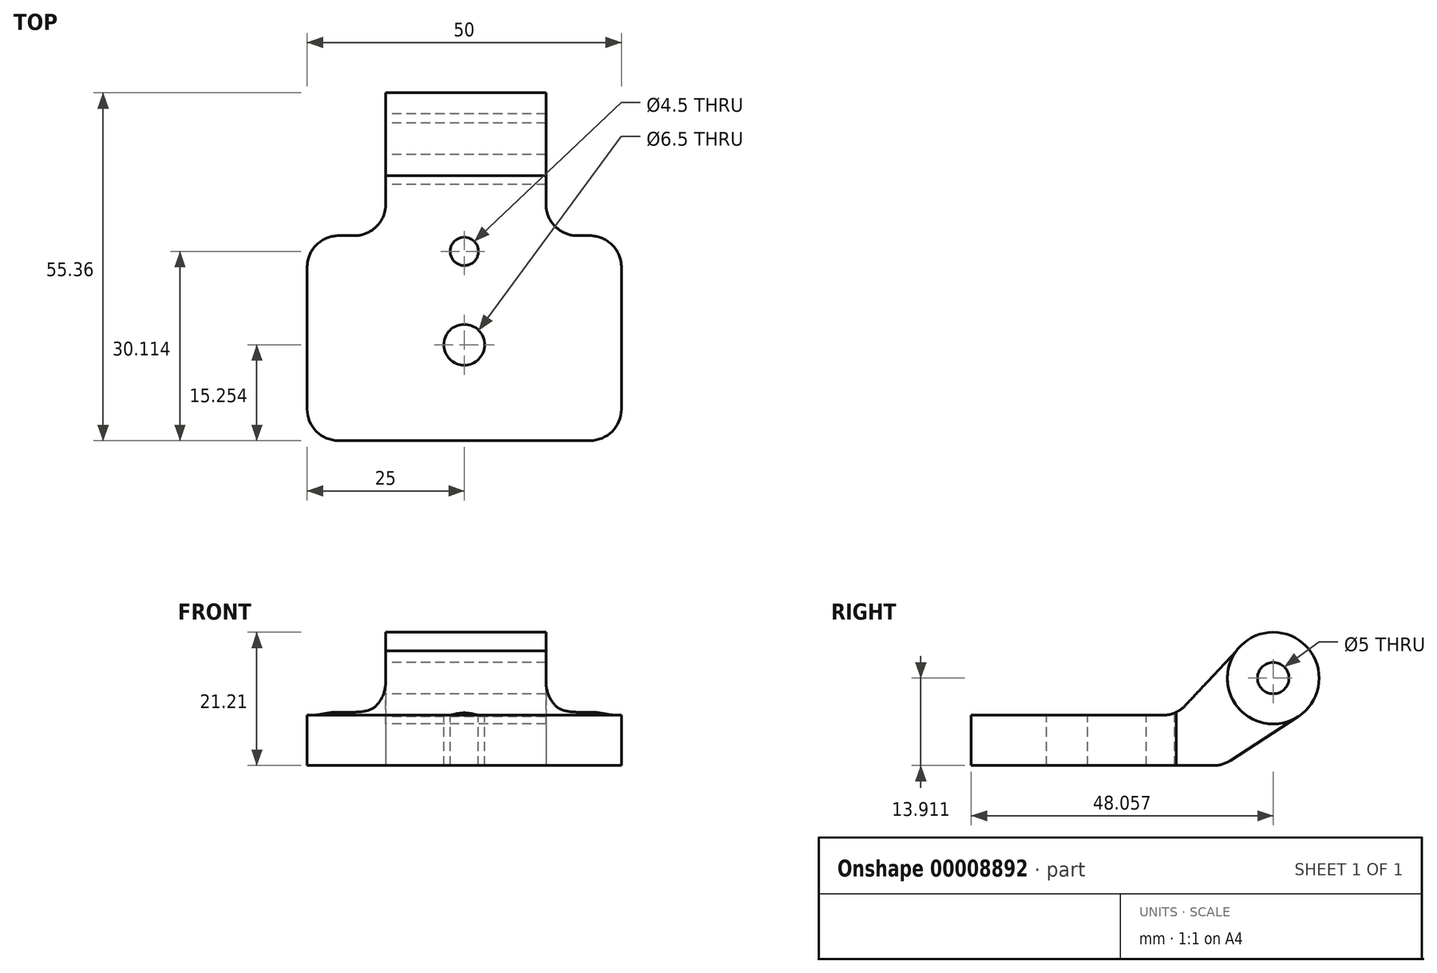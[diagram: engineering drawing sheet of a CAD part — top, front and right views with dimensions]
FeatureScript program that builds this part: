
annotation { "Feature Type Name" : "Feature", "Feature Type Description" : "" }
export const myFeature = defineFeature(function(context is Context, id is Id, definition is map)
    precondition{}
    {
        {
            var Q0;
            Q0=qCreatedBy(makeId("Right.planeOp"),FACE);
            var sketch = newSketch(context, id + "F0", { "sketchPlane" : qUnion([Q0])});
            skCircle(sketch, "E0", {"center": v(-11.81, 6.81) * mm, "radius": 7.3 * mm});
            skCircle(sketch, "E1", {"center": v(-11.81, 6.81) * mm, "radius": 2.5 * mm});
            skSolve(sketch);
        }
        {
            var Q0;
            Q0=makeQuery(id+"F0.imprint","IMPRINT",FACE,{"disambiguationData":[TD([[makeQuery(id+"F0.imprint","IMPRINT",EDGE,{"derivedFrom":sQuery(id+"F0.wireOp",EDGE,"E0")}),1.0]])]});
            extrude(context, id + "F1", {"entities" : qUnion([Q0]), "depth" : 25.5 * mm});
        }
        {
            var Q0;
            Q0=makeQuery(id+"F1.opExtrude","CAP_FACE",FACE,{"disambiguationData":[OSD([sQuery(id+"F0.wireOp",EDGE,"E0"),sQuery(id+"F0.wireOp",EDGE,"E1")])],"isStart":true});
            var sketch = newSketch(context, id + "F2", { "sketchPlane" : qUnion([Q0])});
            skLineSegment(sketch, "E2", {"start": v(7.88, 0.66) * mm, "end": v(19.87, -7.1) * mm});
            skLineSegment(sketch, "E3", {"start": v(19.87, -7.1) * mm, "end": v(59.87, -7.1) * mm});
            skLineSegment(sketch, "E4", {"start": v(59.87, -7.1) * mm, "end": v(59.87, 0.9) * mm});
            skLineSegment(sketch, "E5", {"start": v(59.87, 0.9) * mm, "end": v(27.25, 0.9) * mm});
            skLineSegment(sketch, "E6", {"start": v(27.25, 0.9) * mm, "end": v(17.68, 11.15) * mm});
            skLineSegment(sketch, "E7", {"start": v(27.25, 0.9) * mm, "end": v(27.25, -7.1) * mm});
            skSolve(sketch);
        }
        {
            var Q0;
            {var subQ2=sQuery(id+"F2.wireOp",EDGE,"E2");Q0=makeQuery(id+"F2.imprint","IMPRINT",FACE,{"disambiguationData":[TD([[makeQuery(id+"F2.imprint","IMPRINT",EDGE,{"derivedFrom":subQ2}),1.0]])]});}
            extrude(context, id + "F3", {"entities" : qUnion([Q0]), "oppositeDirection" : true, "depth" : 25.5 * mm});
        }
        {
            var Q0;
            Q0 = qSketchRegion(id + "F2", true);
            extrude(context, id + "F4", {"entities" : qUnion([Q0]), "oppositeDirection" : true, "depth" : 37.5 * mm});
        }
        {
            var Q0;
            {var subQ1=sQuery(id+"F2.wireOp",EDGE,"E4");Q0=makeQuery(id+"F2.imprint","IMPRINT",FACE,{"disambiguationData":[TD([[makeQuery(id+"F2.imprint","IMPRINT",EDGE,{"derivedFrom":subQ1}),1.0]])]});}
            extrude(context, id + "F5", {"entities" : qUnion([Q0]), "operationType" : NewBodyOperationType.ADD, "depth" : 12.5 * mm});
        }
        {
            var Q0;
            {var subQ0=sQuery(id+"F2.wireOp",EDGE,"E5");Q0=makeQuery(id+"F5.boolean.opBoolean","MERGE",FACE,{"derivedFrom":[makeQuery(id+"F4.opExtrude","SWEPT_FACE",FACE,{"disambiguationData":[OSD([subQ0])]}),makeQuery(id+"F5.opExtrude","SWEPT_FACE",FACE,{"disambiguationData":[OSD([subQ0])]})]});}
            var sketch = newSketch(context, id + "F6", { "sketchPlane" : qUnion([Q0])});
            skCircle(sketch, "E8", {"center": v(12.5, -44.62) * mm, "radius": 3.25 * mm});
            skCircle(sketch, "E9", {"center": v(12.5, -29.76) * mm, "radius": 2.25 * mm});
            skSolve(sketch);
        }
        {
            var Q0;
            Q0 = qSketchRegion(id + "F6", true);
            extrude(context, id + "F7", {"entities" : qUnion([Q0]), "operationType" : NewBodyOperationType.REMOVE, "endBound" : BoundingType.THROUGH_ALL, "oppositeDirection" : true, "depth" : 25 * mm});
        }
        {
            var Q0;
            Q0=makeQuery(id+"F5.opExtrude","CAP_EDGE",EDGE,{"disambiguationData":[OSD([sQuery(id+"F2.wireOp",EDGE,"E7")])],"isStart":false});
            var Q1;
            Q1=makeQuery(id+"F4.opExtrude","CAP_EDGE",EDGE,{"disambiguationData":[OSD([sQuery(id+"F2.wireOp",EDGE,"E7")])],"isStart":false});
            var Q2;
            {var subQ0=sQuery(id+"F2.wireOp",EDGE,"E5");var subQ1=sQuery(id+"F2.wireOp",EDGE,"E6");var subQ2=sQuery(id+"F2.wireOp",EDGE,"E7");Q2=makeQuery(id+"F5.boolean.opBoolean","MERGE",EDGE,{"derivedFrom":[makeQuery(id+"F3.opExtrude","SWEPT_EDGE",EDGE,{"disambiguationData":[OSD([subQ0,subQ1,subQ2])]}),makeQuery(id+"F4.opExtrude","SWEPT_EDGE",EDGE,{"disambiguationData":[OSD([subQ0,subQ1,subQ2])]}),makeQuery(id+"F5.opExtrude","SWEPT_EDGE",EDGE,{"disambiguationData":[OSD([subQ0,subQ1,subQ2])]})]});}
            var Q3;
            Q3=makeQuery(id+"F3.opExtrude","SWEPT_EDGE",EDGE,{"disambiguationData":[OSD([sQuery(id+"F2.wireOp",EDGE,"E2"),sQuery(id+"F2.wireOp",EDGE,"E3")])]});
            var Q4;
            Q4=makeQuery(id+"F3.opExtrude","CAP_EDGE",EDGE,{"disambiguationData":[OSD([sQuery(id+"F2.wireOp",EDGE,"E7")])],"isStart":true});
            var Q5;
            Q5=makeQuery(id+"F3.opExtrude","CAP_EDGE",EDGE,{"disambiguationData":[OSD([sQuery(id+"F2.wireOp",EDGE,"E7")])],"isStart":false});
            var Q6;
            Q6=makeQuery(id+"F5.opExtrude","CAP_EDGE",EDGE,{"disambiguationData":[OSD([sQuery(id+"F2.wireOp",EDGE,"E4")])],"isStart":false});
            var Q7;
            Q7=makeQuery(id+"F4.opExtrude","CAP_EDGE",EDGE,{"disambiguationData":[OSD([sQuery(id+"F2.wireOp",EDGE,"E4")])],"isStart":false});
            fillet(context, id + "F8", {"entities" : qUnion([Q0, Q1, Q2, Q3, Q4, Q5, Q6, Q7]), "radius" : 5 * mm, "tangentPropagation" : true, "allowEdgeOverflow" : false});
        }
    });
